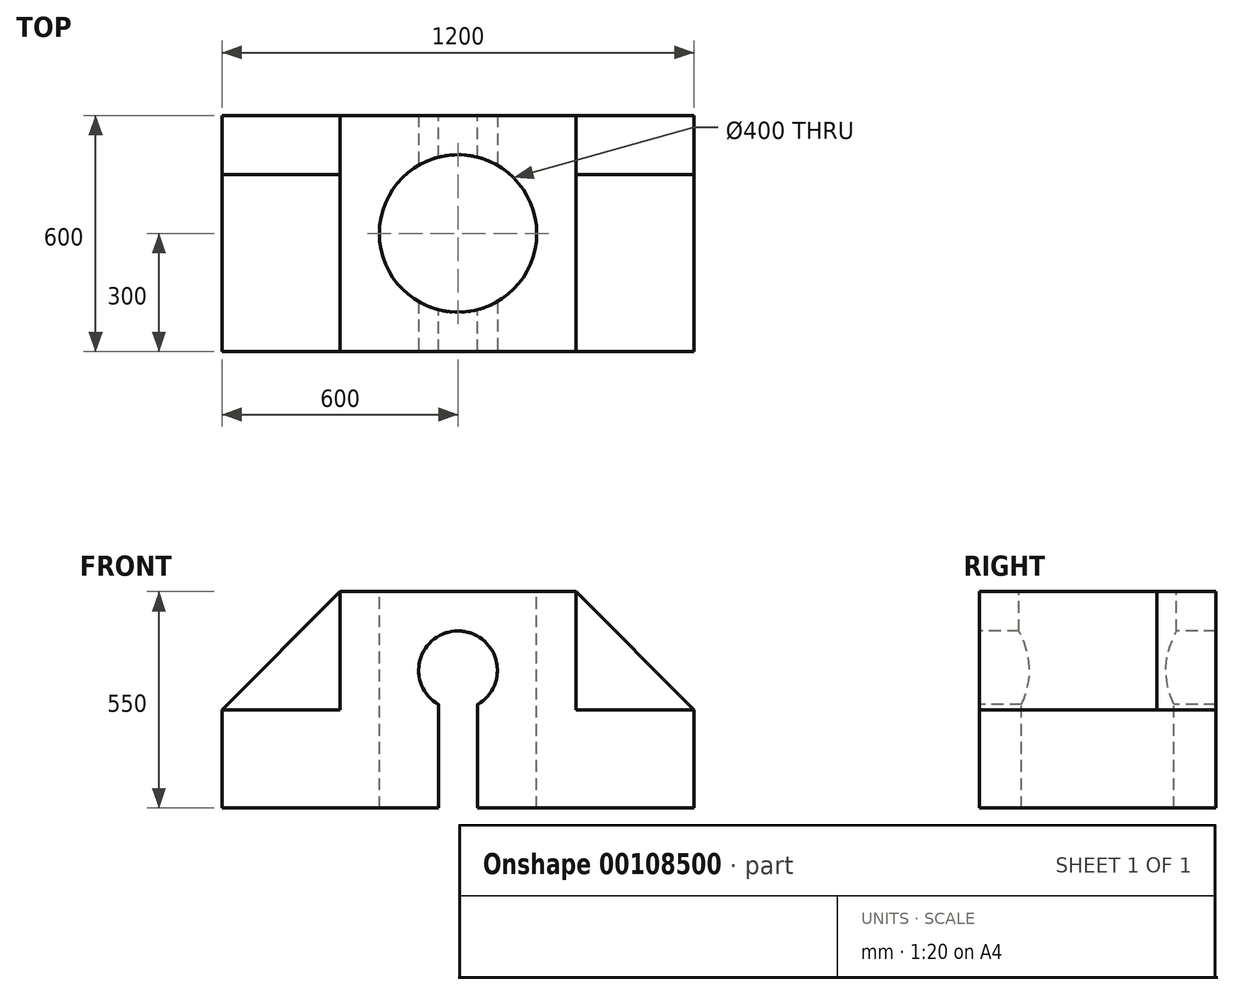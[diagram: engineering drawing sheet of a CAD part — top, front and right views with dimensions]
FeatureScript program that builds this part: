
annotation { "Feature Type Name" : "Feature", "Feature Type Description" : "" }
export const myFeature = defineFeature(function(context is Context, id is Id, definition is map)
    precondition{}
    {
        {
            var Q0;
            Q0=qCreatedBy(makeId("Front.planeOp"),FACE);
            var sketch = newSketch(context, id + "F0", { "sketchPlane" : qUnion([Q0])});
            skLineSegment(sketch, "E0.bottom", {"start": v(600, -275) * mm, "end": v(-600, -275) * mm});
            skLineSegment(sketch, "E0.top", {"start": v(600, 275) * mm, "end": v(-600, 275) * mm});
            skLineSegment(sketch, "E0.left", {"start": v(600, -275) * mm, "end": v(600, 275) * mm});
            skLineSegment(sketch, "E0.right", {"start": v(-600, -275) * mm, "end": v(-600, 275) * mm});
            skPoint(sketch, "E0.middle", {"position": v(0, 0) * mm});
            skSolve(sketch);
        }
        {
            var Q0;
            Q0 = qSketchRegion(id + "F0", true);
            extrude(context, id + "F1", {"entities" : qUnion([Q0]), "depth" : 600 * mm});
        }
        {
            var Q0;
            Q0=makeQuery(id+"F1.opExtrude","CAP_FACE",FACE,{"disambiguationData":[OSD([sQuery(id+"F0.wireOp",EDGE,"E0.bottom"),sQuery(id+"F0.wireOp",EDGE,"E0.top"),sQuery(id+"F0.wireOp",EDGE,"E0.left"),sQuery(id+"F0.wireOp",EDGE,"E0.right")])],"isStart":false});
            var sketch = newSketch(context, id + "F2", { "sketchPlane" : qUnion([Q0])});
            skLineSegment(sketch, "E1.bottom", {"start": v(-600, 275) * mm, "end": v(-300, 275) * mm});
            skLineSegment(sketch, "E1.top", {"start": v(-600, -25) * mm, "end": v(-300, -25) * mm});
            skLineSegment(sketch, "E1.left", {"start": v(-600, 275) * mm, "end": v(-600, -25) * mm});
            skLineSegment(sketch, "E1.right", {"start": v(-300, 275) * mm, "end": v(-300, -25) * mm});
            skLineSegment(sketch, "E2.bottom", {"start": v(600, 275) * mm, "end": v(300, 275) * mm});
            skLineSegment(sketch, "E2.top", {"start": v(600, -25) * mm, "end": v(300, -25) * mm});
            skLineSegment(sketch, "E2.left", {"start": v(600, 275) * mm, "end": v(600, -25) * mm});
            skLineSegment(sketch, "E2.right", {"start": v(300, 275) * mm, "end": v(300, -25) * mm});
            skSolve(sketch);
        }
        {
            var Q0;
            Q0 = qSketchRegion(id + "F2", true);
            extrude(context, id + "F3", {"entities" : qUnion([Q0]), "operationType" : NewBodyOperationType.REMOVE, "endBound" : BoundingType.THROUGH_ALL, "oppositeDirection" : true, "depth" : 25 * mm});
        }
        {
            var Q0;
            Q0=makeQuery(id+"F1.opExtrude","CAP_FACE",FACE,{"disambiguationData":[OSD([sQuery(id+"F0.wireOp",EDGE,"E0.bottom"),sQuery(id+"F0.wireOp",EDGE,"E0.top"),sQuery(id+"F0.wireOp",EDGE,"E0.left"),sQuery(id+"F0.wireOp",EDGE,"E0.right")])],"isStart":true});
            var sketch = newSketch(context, id + "F4", { "sketchPlane" : qUnion([Q0])});
            skLineSegment(sketch, "E3", {"start": v(-300, 275) * mm, "end": v(-600, -25) * mm});
            skLineSegment(sketch, "E4", {"start": v(300, 275) * mm, "end": v(600, -25) * mm});
            skSolve(sketch);
        }
        {
            var Q0;
            Q0 = qSketchRegion(id + "F4", true);
            var Q1;
            Q1=makeQuery(id+"F4.imprint","IMPRINT",FACE,{"disambiguationData":[TD([[makeQuery(id+"F4.imprint","IMPRINT",EDGE,{"derivedFrom":sQuery(id+"F4.wireOp",EDGE,"E3")}),1.0]])]});
            var Q2;
            Q2=makeQuery(id+"F4.imprint","IMPRINT",FACE,{"disambiguationData":[TD([[makeQuery(id+"F4.imprint","IMPRINT",EDGE,{"derivedFrom":sQuery(id+"F4.wireOp",EDGE,"E4")}),-1.0]])]});
            extrude(context, id + "F5", {"entities" : qUnion([Q0, Q1, Q2]), "operationType" : NewBodyOperationType.ADD, "oppositeDirection" : true, "depth" : 150 * mm});
        }
        {
            var Q0;
            Q0=makeQuery(id+"F1.opExtrude","SWEPT_FACE",FACE,{"disambiguationData":[OSD([sQuery(id+"F0.wireOp",EDGE,"E0.top")])]});
            var sketch = newSketch(context, id + "F6", { "sketchPlane" : qUnion([Q0])});
            skCircle(sketch, "E5", {"center": v(0, -300) * mm, "radius": 200 * mm});
            skSolve(sketch);
        }
        {
            var Q0;
            Q0 = qSketchRegion(id + "F6", true);
            var Q1;
            Q1=makeQuery(id+"F6.imprint","IMPRINT",FACE,{"disambiguationData":[TD([[makeQuery(id+"F6.imprint","IMPRINT",EDGE,{"derivedFrom":sQuery(id+"F6.wireOp",EDGE,"E5")}),1.0]])]});
            extrude(context, id + "F7", {"entities" : qUnion([Q0, Q1]), "operationType" : NewBodyOperationType.REMOVE, "endBound" : BoundingType.THROUGH_ALL, "oppositeDirection" : true, "depth" : 25 * mm});
        }
        {
            var Q0;
            Q0=makeQuery(id+"F1.opExtrude","CAP_FACE",FACE,{"disambiguationData":[OSD([sQuery(id+"F0.wireOp",EDGE,"E0.bottom"),sQuery(id+"F0.wireOp",EDGE,"E0.top"),sQuery(id+"F0.wireOp",EDGE,"E0.left"),sQuery(id+"F0.wireOp",EDGE,"E0.right")])],"isStart":false});
            var sketch = newSketch(context, id + "F8", { "sketchPlane" : qUnion([Q0])});
            skPoint(sketch, "E6.endSnap0", {"position": v(0, -275) * mm});
            skCircle(sketch, "E7", {"center": v(0, 75) * mm, "radius": 100 * mm});
            skPoint(sketch, "E8.orphan", {"position": v(0, 275) * mm});
            skLineSegment(sketch, "E9.bottom", {"start": v(50, 75) * mm, "end": v(-50, 75) * mm});
            skLineSegment(sketch, "E9.top", {"start": v(50, -625) * mm, "end": v(-50, -625) * mm});
            skLineSegment(sketch, "E9.left", {"start": v(50, 75) * mm, "end": v(50, -625) * mm});
            skLineSegment(sketch, "E9.right", {"start": v(-50, 75) * mm, "end": v(-50, -625) * mm});
            skSolve(sketch);
        }
        {
            var Q0;
            Q0 = qSketchRegion(id + "F8", true);
            extrude(context, id + "F9", {"entities" : qUnion([Q0]), "operationType" : NewBodyOperationType.REMOVE, "endBound" : BoundingType.THROUGH_ALL, "oppositeDirection" : true, "depth" : 25 * mm});
        }
    });
